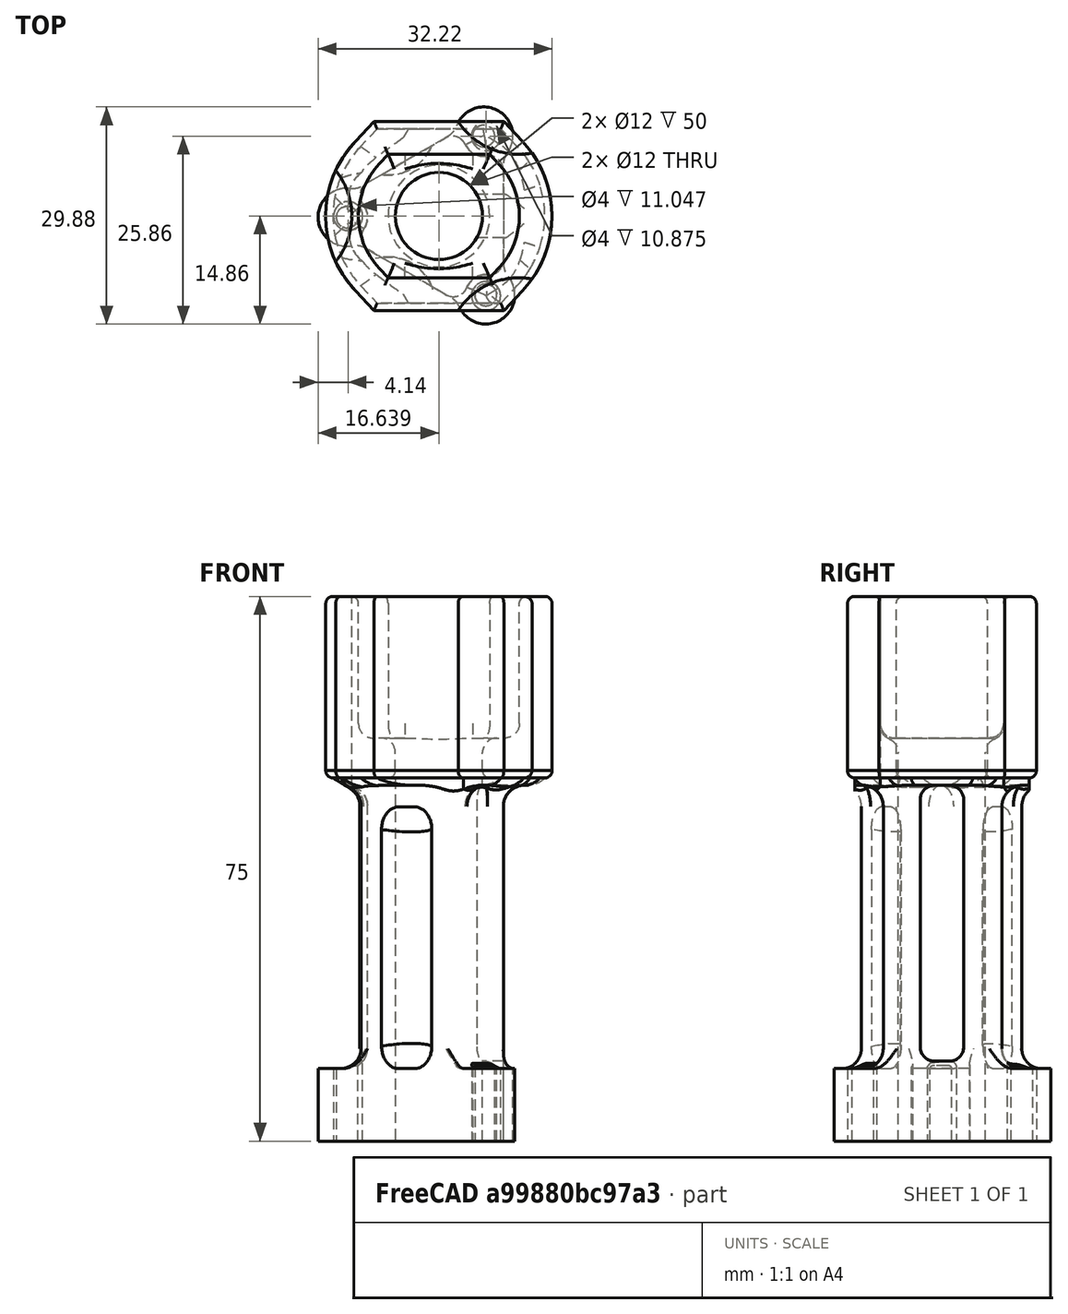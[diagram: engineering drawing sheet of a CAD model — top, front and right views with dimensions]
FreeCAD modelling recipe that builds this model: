
FCSTD DOCUMENT  (FreeCAD 0.21R33771 (Git))
Label: stirring-mount-screws-accessible
License: All rights reserved
LicenseURL: https://en.wikipedia.org/wiki/All_rights_reserved
objects: Part::Cylinder×6, Part::Cut×6, Part::Feature×2, App::Part×1, Part::FeaturePython×1
note: 15 computed .brp shape members not serialized (recipe doc carries the construction recipe); baked Part::Feature solids carry a one-line shape summary decoded from their .brp

FEATURE [Part::Feature] Part__Feature  label="Stirring v21"
  shape: bbox 33.64 x 32.9 x 52.01 mm, 107 faces (baked)
FEATURE [Part::Feature] Part__Feature001  label="Stirring v022"
  shape: bbox 33.63 x 26 x 24 mm, 50 faces (baked)
FEATURE [App::Part] Stirring_v21  label="Stirring v023"
  Group = -> [Part__Feature,Part__Feature001]
  Origin = -> Origin
FEATURE [Part::Cylinder] Cylinder  label="Screw Hole Cut 1"
  Angle = 360
  AttacherType = Attacher::AttachEngine3D
  FirstAngle = 0
  Height = 20
  Placement = pos=(87,106,459) rot=(0,0,1;0rad)
  Radius = 2
  SecondAngle = 0
FEATURE [Part::FeaturePython] Clone  label="Stirring v024"  # Draft clone (typed FeaturePython)
  AttacherType = Attacher::AttachEngine3D
  Fuse = false
  Objects = -> [Stirring_v21]
  Scale = (1,1,1)
FEATURE [Part::Cylinder] Cylinder001  label="Screw Hole Cut 002"
  Angle = 360
  AttacherType = Attacher::AttachEngine3D
  FirstAngle = 0
  Height = 20
  Placement = pos=(87,128,459) rot=(0,0,1;0rad)
  Radius = 2
  SecondAngle = 0
FEATURE [Part::Cylinder] Cylinder002  label="Screw Hole Cut 003"
  Angle = 360
  AttacherType = Attacher::AttachEngine3D
  FirstAngle = 0
  Height = 20
  Placement = pos=(68,117,459) rot=(0,0,1;0rad)
  Radius = 2
  SecondAngle = 0
FEATURE [Part::Cylinder] Cylinder003  label="Screwdriver-accessibility cut1"
  Angle = 360
  AttacherType = Attacher::AttachEngine3D
  FirstAngle = 0
  Height = 30
  Placement = pos=(91.5,98.5,506) rot=(0,0,1;0rad)
  Radius = 10
  SecondAngle = 0
FEATURE [Part::Cylinder] Cylinder004  label="Screwdriver-accessibility cut2"
  Angle = 360
  AttacherType = Attacher::AttachEngine3D
  FirstAngle = 0
  Height = 30
  Placement = pos=(91.5,135.5,505) rot=(0,0,1;0rad)
  Radius = 10
  SecondAngle = 0
FEATURE [Part::Cylinder] Cylinder005  label="Screwdriver-accessibility cut3"
  Angle = 360
  AttacherType = Attacher::AttachEngine3D
  FirstAngle = 0
  Height = 30
  Placement = pos=(58.5,117,506) rot=(0,0,1;0rad)
  Radius = 10
  SecondAngle = 0
FEATURE [Part::Cut] Cut
  Base = -> Clone
  Tool = -> Cylinder003
FEATURE [Part::Cut] Cut001
  Base = -> Cut
  Tool = -> Cylinder004
FEATURE [Part::Cut] Cut002  label="Motor Stand more accessible"
  Base = -> Cut001
  Tool = -> Cylinder005
FEATURE [Part::Cut] Cut003
  Base = -> Cut002
  Tool = -> Cylinder002
FEATURE [Part::Cut] Cut004
  Base = -> Cut003
  Tool = -> Cylinder001
FEATURE [Part::Cut] Cut005  label="Stirring Mount with accessible screws"
  Base = -> Cut004
  Tool = -> Cylinder
